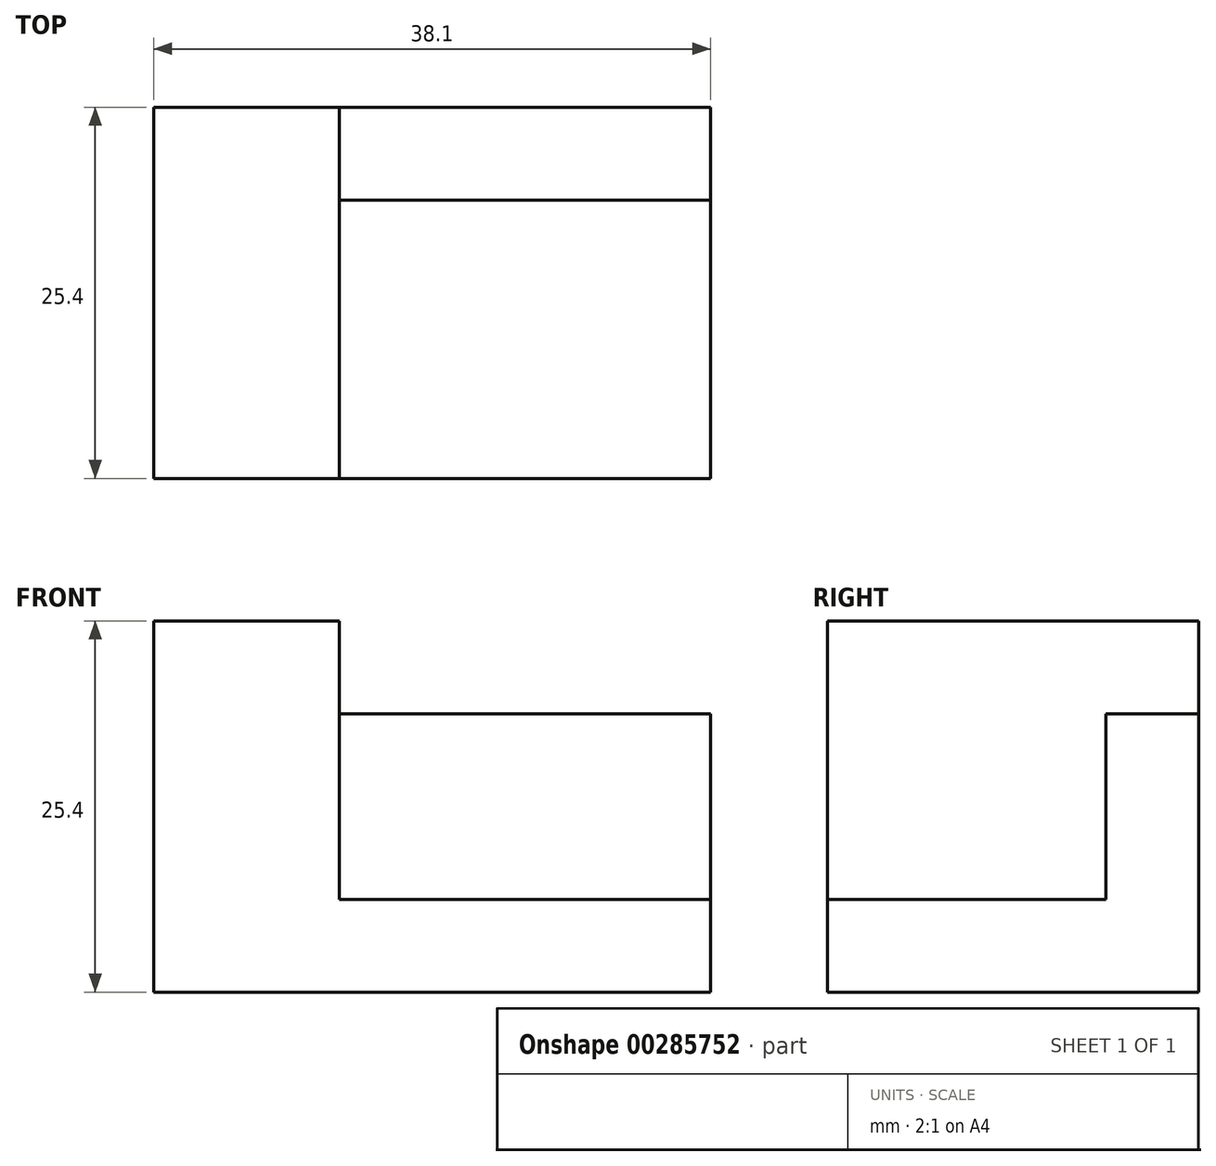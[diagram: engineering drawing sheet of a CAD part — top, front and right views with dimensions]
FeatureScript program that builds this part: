
annotation { "Feature Type Name" : "Feature", "Feature Type Description" : "" }
export const myFeature = defineFeature(function(context is Context, id is Id, definition is map)
    precondition{}
    {
        {
            var Q0;
            Q0=qCreatedBy(makeId("Top.planeOp"),FACE);
            var sketch = newSketch(context, id + "F0", { "sketchPlane" : qUnion([Q0])});
            skLineSegment(sketch, "E0.bottom", {"start": v(0, 0) * mm, "end": v(38.1, 0) * mm});
            skLineSegment(sketch, "E0.top", {"start": v(0, 25.4) * mm, "end": v(38.1, 25.4) * mm});
            skLineSegment(sketch, "E0.left", {"start": v(0, 0) * mm, "end": v(0, 25.4) * mm});
            skLineSegment(sketch, "E0.right", {"start": v(38.1, 0) * mm, "end": v(38.1, 25.4) * mm});
            skSolve(sketch);
        }
        {
            var Q0;
            Q0 = qSketchRegion(id + "F0", true);
            extrude(context, id + "F1", {"entities" : qUnion([Q0]), "oppositeDirection" : true, "depth" : 25.4 * mm});
        }
        {
            var Q0;
            Q0=qCreatedBy(makeId("Top.planeOp"),FACE);
            var sketch = newSketch(context, id + "F2", { "sketchPlane" : qUnion([Q0])});
            skLineSegment(sketch, "E1.bottom", {"start": v(38.1, 0) * mm, "end": v(12.7, 0) * mm});
            skLineSegment(sketch, "E1.top", {"start": v(38.1, 19.05) * mm, "end": v(12.7, 19.05) * mm});
            skLineSegment(sketch, "E1.left", {"start": v(38.1, 0) * mm, "end": v(38.1, 19.05) * mm});
            skLineSegment(sketch, "E1.right", {"start": v(12.7, 0) * mm, "end": v(12.7, 19.05) * mm});
            skSolve(sketch);
        }
        {
            var Q0;
            Q0 = qSketchRegion(id + "F2", true);
            extrude(context, id + "F3", {"entities" : qUnion([Q0]), "operationType" : NewBodyOperationType.REMOVE, "oppositeDirection" : true, "depth" : 19.05 * mm});
        }
        {
            var Q0;
            Q0=qCreatedBy(makeId("Top.planeOp"),FACE);
            var sketch = newSketch(context, id + "F4", { "sketchPlane" : qUnion([Q0])});
            skLineSegment(sketch, "E2.bottom", {"start": v(12.7, 25.4) * mm, "end": v(38.1, 25.4) * mm});
            skLineSegment(sketch, "E2.top", {"start": v(12.7, 19.05) * mm, "end": v(38.1, 19.05) * mm});
            skLineSegment(sketch, "E2.left", {"start": v(12.7, 25.4) * mm, "end": v(12.7, 19.05) * mm});
            skLineSegment(sketch, "E2.right", {"start": v(38.1, 25.4) * mm, "end": v(38.1, 19.05) * mm});
            skSolve(sketch);
        }
        {
            var Q0;
            Q0 = qSketchRegion(id + "F4", true);
            extrude(context, id + "F5", {"entities" : qUnion([Q0]), "operationType" : NewBodyOperationType.REMOVE, "oppositeDirection" : true, "depth" : 6.35 * mm});
        }
    });
